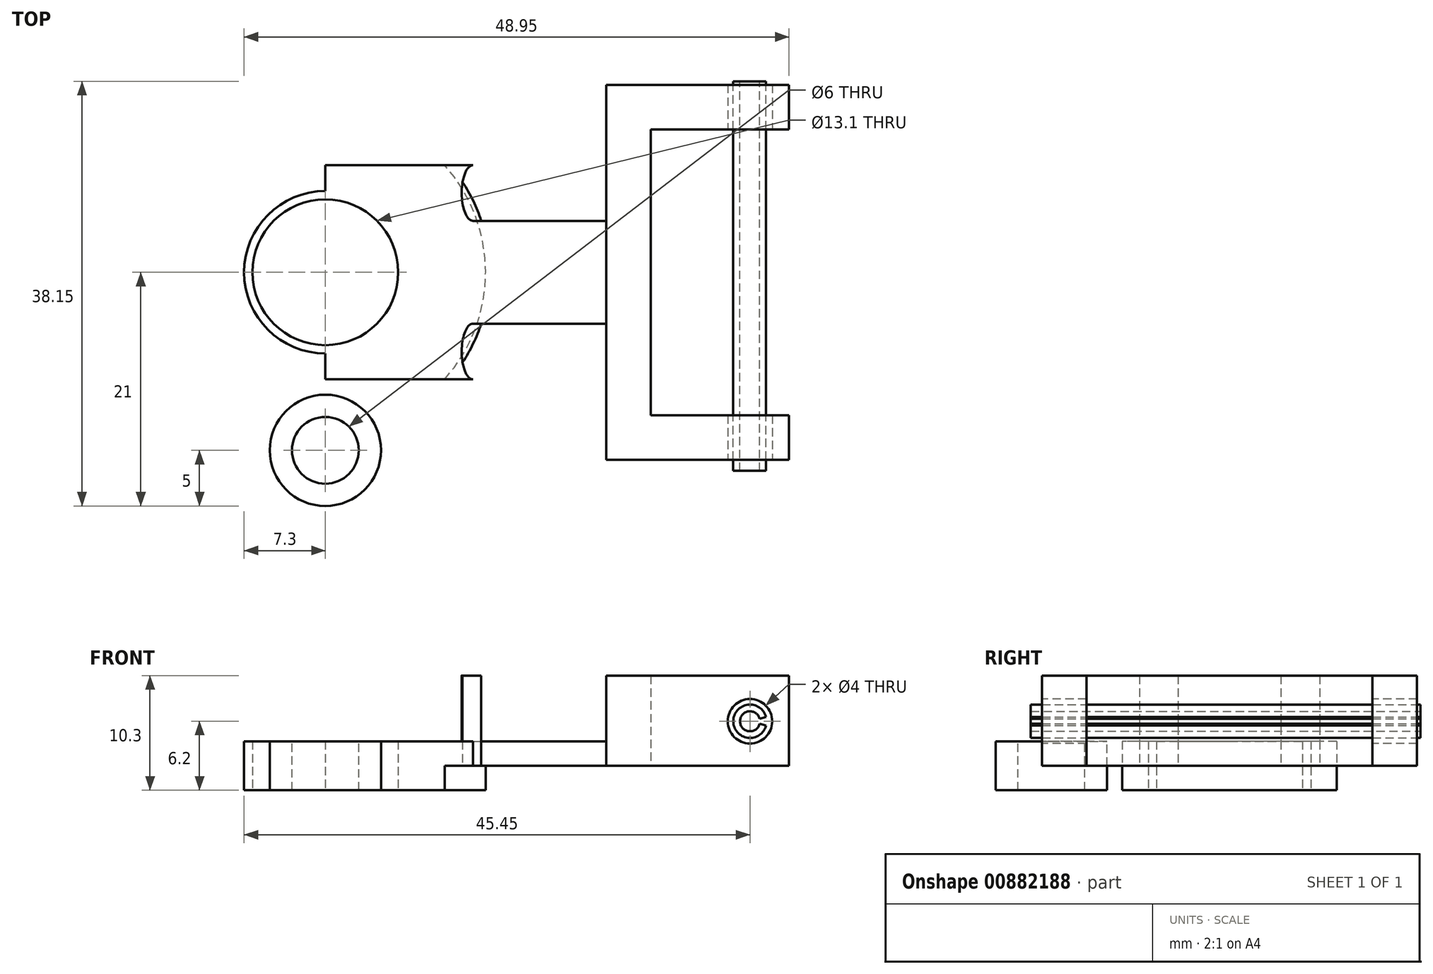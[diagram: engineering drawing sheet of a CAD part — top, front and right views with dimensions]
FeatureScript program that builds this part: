
annotation { "Feature Type Name" : "Feature", "Feature Type Description" : "" }
export const myFeature = defineFeature(function(context is Context, id is Id, definition is map)
    precondition{}
    {
        {
            var Q0;
            Q0=qCreatedBy(makeId("Top.planeOp"),FACE);
            var sketch = newSketch(context, id + "F0", { "sketchPlane" : qUnion([Q0])});
            skCircle(sketch, "E0", {"center": v(0, 0) * mm, "radius": 14.75 * mm});
            skCircle(sketch, "E1", {"center": v(0, 0) * mm, "radius": 14.4 * mm});
            skCircle(sketch, "E2", {"center": v(0, 0) * mm, "radius": 6.55 * mm});
            skCircle(sketch, "E3", {"center": v(0, 0) * mm, "radius": 7.3 * mm});
            skLineSegment(sketch, "E4", {"start": v(0, 0) * mm, "end": v(48.92, 0) * mm, "construction": true});
            skLineSegment(sketch, "E5.bottom", {"start": v(0, 9.62) * mm, "end": v(25.25, 9.62) * mm});
            skLineSegment(sketch, "E5.top", {"start": v(0, -9.62) * mm, "end": v(25.25, -9.62) * mm});
            skLineSegment(sketch, "E5.left", {"start": v(0, 9.62) * mm, "end": v(0, -9.62) * mm});
            skPoint(sketch, "E5.middle", {"position": v(12.63, 0) * mm});
            skLineSegment(sketch, "E6.bottom", {"start": v(25.25, 16.85) * mm, "end": v(41.65, 16.85) * mm});
            skLineSegment(sketch, "E6.top", {"start": v(25.25, -16.85) * mm, "end": v(41.65, -16.85) * mm});
            skLineSegment(sketch, "E6.left", {"start": v(25.25, 16.85) * mm, "end": v(25.25, 9.62) * mm});
            skLineSegment(sketch, "E6.right", {"start": v(41.65, 16.85) * mm, "end": v(41.65, 12.85) * mm});
            skPoint(sketch, "E6.middle", {"position": v(33.45, 0) * mm});
            skLineSegment(sketch, "E7.bottom", {"start": v(29.25, -12.85) * mm, "end": v(41.65, -12.85) * mm});
            skLineSegment(sketch, "E7.top", {"start": v(29.25, 12.85) * mm, "end": v(41.65, 12.85) * mm});
            skLineSegment(sketch, "E7.left", {"start": v(29.25, -12.85) * mm, "end": v(29.25, 12.85) * mm});
            skLineSegment(sketch, "E8.trimOffspring", {"start": v(41.65, -12.85) * mm, "end": v(41.65, -16.85) * mm});
            skLineSegment(sketch, "E9.trimOffspring", {"start": v(25.25, -9.62) * mm, "end": v(25.25, -16.85) * mm});
            skLineSegment(sketch, "E10.bottom", {"start": v(25.25, 9.62) * mm, "end": v(13.25, 9.62) * mm});
            skLineSegment(sketch, "E10.top", {"start": v(25.25, 4.62) * mm, "end": v(13.25, 4.62) * mm});
            skLineSegment(sketch, "E10.left", {"start": v(25.25, 9.62) * mm, "end": v(25.25, 4.62) * mm});
            skLineSegment(sketch, "E10.right", {"start": v(13.25, 9.62) * mm, "end": v(13.25, 4.62) * mm, "construction": true});
            skPoint(sketch, "E11", {"position": v(10.71, 9.63) * mm});
            skPoint(sketch, "E12", {"position": v(11.18, 9.62) * mm});
            skPoint(sketch, "E13", {"position": v(10.71, -9.62) * mm});
            skPoint(sketch, "E14", {"position": v(11.18, -9.62) * mm});
            skLineSegment(sketch, "E15", {"start": v(0, 0) * mm, "end": v(-14.4, 0) * mm, "construction": true});
            skLineSegment(sketch, "E16", {"start": v(-14.4, 0) * mm, "end": v(-14.75, 0) * mm, "construction": true});
            skArc(sketch, "E17", {"start": v(10.71, 9.63) * mm, "mid": v(-14.4, 0) * mm, "end": v(10.71, -9.63) * mm});
            skArc(sketch, "E18", {"start": v(11.18, 9.62) * mm, "mid": v(-14.75, 0) * mm, "end": v(11.18, -9.63) * mm});
            skEllipticalArc(sketch, "E19", {});
            skLineSegment(sketch, "E20.MirrorCS", {"start": v(25.25, -4.62) * mm, "end": v(13.25, -4.62) * mm});
            skEllipticalArc(sketch, "E21.MirrorCS", {});
            skLineSegment(sketch, "E22.MirrorCS", {"start": v(25.25, -9.62) * mm, "end": v(13.25, -9.62) * mm});
            skLineSegment(sketch, "E23.MirrorCS", {"start": v(25.25, -9.62) * mm, "end": v(25.25, -4.62) * mm});
            skLineSegment(sketch, "E24", {"start": v(25.25, 4.62) * mm, "end": v(25.25, -4.62) * mm});
            const initialGuessF0  = {"E19": [0.01325, 0.007125, 0, 1, 0.0025, 0.001, 0, 3.141592653589793], "E21.MirrorCS": [0.01325, -0.007125, 0, -1, 0.0025, 0.001, 3.141592653589793, 0]};
            skSetInitialGuess(sketch, initialGuessF0);
            skSolve(sketch);
        }
        {
            var Q0;
            {var subQ0=sQuery(id+"F0.wireOp",EDGE,"E19");var subQ1=sQuery(id+"F0.wireOp",EDGE,"E0");var subQ2=makeQuery(id+"F0.imprint","INTERSECT",VERTEX,{"derivedFrom":[subQ1,subQ0]});Q0=makeQuery(id+"F0.imprint","IMPRINT",FACE,{"disambiguationData":[TD([[makeQuery(id+"F0.imprint","IMPRINT",EDGE,{"disambiguationData":[TD([[subQ2,1.0]])],"derivedFrom":subQ1}),1.0]])]});}
            var Q1;
            {var subQ0=sQuery(id+"F0.wireOp",EDGE,"E5.bottom");var subQ1=sQuery(id+"F0.wireOp",EDGE,"E0");var subQ2=makeQuery(id+"F0.imprint","INTERSECT",VERTEX,{"derivedFrom":[subQ1,subQ0]});Q1=makeQuery(id+"F0.imprint","IMPRINT",FACE,{"disambiguationData":[TD([[makeQuery(id+"F0.imprint","IMPRINT",EDGE,{"disambiguationData":[TD([[subQ2,1.0]])],"derivedFrom":subQ1}),1.0]])]});}
            var Q2;
            {var subQ0=sQuery(id+"F0.wireOp",EDGE,"E10.top");var subQ1=sQuery(id+"F0.wireOp",EDGE,"E0");var subQ2=makeQuery(id+"F0.imprint","INTERSECT",VERTEX,{"derivedFrom":[subQ1,subQ0]});Q2=makeQuery(id+"F0.imprint","IMPRINT",FACE,{"disambiguationData":[TD([[makeQuery(id+"F0.imprint","IMPRINT",EDGE,{"disambiguationData":[TD([[subQ2,1.0]])],"derivedFrom":subQ1}),1.0]])]});}
            var Q3;
            {var subQ0=sQuery(id+"F0.wireOp",EDGE,"E21.MirrorCS");var subQ1=sQuery(id+"F0.wireOp",EDGE,"E0");var subQ2=makeQuery(id+"F0.imprint","INTERSECT",VERTEX,{"derivedFrom":[subQ1,subQ0]});Q3=makeQuery(id+"F0.imprint","IMPRINT",FACE,{"disambiguationData":[TD([[makeQuery(id+"F0.imprint","IMPRINT",EDGE,{"disambiguationData":[TD([[subQ2,-1.0]])],"derivedFrom":subQ1}),1.0]])]});}
            var Q4;
            {var subQ0=sQuery(id+"F0.wireOp",EDGE,"E5.top");var subQ1=sQuery(id+"F0.wireOp",EDGE,"E0");var subQ2=makeQuery(id+"F0.imprint","INTERSECT",VERTEX,{"derivedFrom":[subQ1,subQ0]});Q4=makeQuery(id+"F0.imprint","IMPRINT",FACE,{"disambiguationData":[TD([[makeQuery(id+"F0.imprint","IMPRINT",EDGE,{"disambiguationData":[TD([[subQ2,-1.0]])],"derivedFrom":subQ1}),1.0]])]});}
            var Q5;
            {var subQ0=sQuery(id+"F0.wireOp",EDGE,"E5.bottom");var subQ1=sQuery(id+"F0.wireOp",EDGE,"E0");var subQ2=makeQuery(id+"F0.imprint","INTERSECT",VERTEX,{"derivedFrom":[subQ1,subQ0]});Q5=makeQuery(id+"F0.imprint","IMPRINT",FACE,{"disambiguationData":[TD([[makeQuery(id+"F0.imprint","IMPRINT",EDGE,{"disambiguationData":[TD([[subQ2,-1.0]])],"derivedFrom":subQ1}),1.0]])]});}
            var Q6;
            {var subQ0=sQuery(id+"F0.wireOp",EDGE,"E19");var subQ3=sQuery(id+"F0.wireOp",EDGE,"E1");var subQ4=makeQuery(id+"F0.imprint","INTERSECT",VERTEX,{"derivedFrom":[subQ3,subQ0]});Q6=makeQuery(id+"F0.imprint","IMPRINT",FACE,{"disambiguationData":[TD([[makeQuery(id+"F0.imprint","IMPRINT",EDGE,{"disambiguationData":[TD([[subQ4,-1.0]])],"derivedFrom":subQ3}),1.0]])]});}
            var Q7;
            {var subQ0=sQuery(id+"F0.wireOp",EDGE,"E19");var subQ1=sQuery(id+"F0.wireOp",EDGE,"E1");var subQ2=makeQuery(id+"F0.imprint","INTERSECT",VERTEX,{"derivedFrom":[subQ1,subQ0]});Q7=makeQuery(id+"F0.imprint","IMPRINT",FACE,{"disambiguationData":[TD([[makeQuery(id+"F0.imprint","IMPRINT",EDGE,{"disambiguationData":[TD([[subQ2,1.0]])],"derivedFrom":subQ1}),1.0]])]});}
            var Q8;
            {var subQ0=sQuery(id+"F0.wireOp",EDGE,"E21.MirrorCS");var subQ1=sQuery(id+"F0.wireOp",EDGE,"E1");var subQ2=makeQuery(id+"F0.imprint","INTERSECT",VERTEX,{"derivedFrom":[subQ1,subQ0]});Q8=makeQuery(id+"F0.imprint","IMPRINT",FACE,{"disambiguationData":[TD([[makeQuery(id+"F0.imprint","IMPRINT",EDGE,{"disambiguationData":[TD([[subQ2,-1.0]])],"derivedFrom":subQ1}),1.0]])]});}
            var Q9;
            {var subQ1=sQuery(id+"F0.wireOp",EDGE,"E5.bottom");var subQ3=sQuery(id+"F0.wireOp",EDGE,"E1");var subQ4=makeQuery(id+"F0.imprint","INTERSECT",VERTEX,{"derivedFrom":[subQ3,subQ1]});Q9=makeQuery(id+"F0.imprint","IMPRINT",FACE,{"disambiguationData":[TD([[makeQuery(id+"F0.imprint","IMPRINT",EDGE,{"disambiguationData":[TD([[subQ4,-1.0]])],"derivedFrom":subQ3}),1.0]])]});}
            var Q10;
            {var subQ0=sQuery(id+"F0.wireOp",EDGE,"E5.left");var subQ1=sQuery(id+"F0.wireOp",EDGE,"E2");var subQ2=makeQuery(id+"F0.imprint","INTERSECT",VERTEX,{"disambiguationData":[OD(0.0)],"derivedFrom":[subQ1,subQ0]});Q10=makeQuery(id+"F0.imprint","IMPRINT",FACE,{"disambiguationData":[TD([[makeQuery(id+"F0.imprint","IMPRINT",EDGE,{"disambiguationData":[TD([[subQ2,-1.0]])],"derivedFrom":subQ1}),-1.0]])]});}
            var Q11;
            {var subQ0=sQuery(id+"F0.wireOp",EDGE,"E5.left");var subQ1=sQuery(id+"F0.wireOp",EDGE,"E2");var subQ2=makeQuery(id+"F0.imprint","INTERSECT",VERTEX,{"disambiguationData":[OD(0.0)],"derivedFrom":[subQ1,subQ0]});Q11=makeQuery(id+"F0.imprint","IMPRINT",FACE,{"disambiguationData":[TD([[makeQuery(id+"F0.imprint","IMPRINT",EDGE,{"disambiguationData":[TD([[subQ2,1.0]])],"derivedFrom":subQ1}),-1.0]])]});}
            extrude(context, id + "F1", {"entities" : qUnion([Q0, Q1, Q2, Q3, Q4, Q5, Q6, Q7, Q8, Q9, Q10, Q11]), "depth" : 2.2 * mm, "offsetDistance" : 25 * mm});
        }
        {
            var Q0;
            Q0=makeQuery(id+"F0.imprint","IMPRINT",FACE,{"disambiguationData":[TD([[makeQuery(id+"F0.imprint","IMPRINT",EDGE,{"derivedFrom":sQuery(id+"F0.wireOp",EDGE,"E1")}),1.0]])]});
            var Q1;
            {var subQ0=sQuery(id+"F0.wireOp",EDGE,"E21.MirrorCS");var subQ1=sQuery(id+"F0.wireOp",EDGE,"E1");var subQ2=makeQuery(id+"F0.imprint","INTERSECT",VERTEX,{"derivedFrom":[subQ1,subQ0]});Q1=makeQuery(id+"F0.imprint","IMPRINT",FACE,{"disambiguationData":[TD([[makeQuery(id+"F0.imprint","IMPRINT",EDGE,{"disambiguationData":[TD([[subQ2,-1.0]])],"derivedFrom":subQ1}),1.0]])]});}
            var Q2;
            {var subQ0=sQuery(id+"F0.wireOp",EDGE,"E19");var subQ1=sQuery(id+"F0.wireOp",EDGE,"E1");var subQ2=makeQuery(id+"F0.imprint","INTERSECT",VERTEX,{"derivedFrom":[subQ1,subQ0]});Q2=makeQuery(id+"F0.imprint","IMPRINT",FACE,{"disambiguationData":[TD([[makeQuery(id+"F0.imprint","IMPRINT",EDGE,{"disambiguationData":[TD([[subQ2,1.0]])],"derivedFrom":subQ1}),1.0]])]});}
            var Q3;
            {var subQ1=sQuery(id+"F0.wireOp",EDGE,"E5.bottom");var subQ3=sQuery(id+"F0.wireOp",EDGE,"E1");var subQ4=makeQuery(id+"F0.imprint","INTERSECT",VERTEX,{"derivedFrom":[subQ3,subQ1]});Q3=makeQuery(id+"F0.imprint","IMPRINT",FACE,{"disambiguationData":[TD([[makeQuery(id+"F0.imprint","IMPRINT",EDGE,{"disambiguationData":[TD([[subQ4,-1.0]])],"derivedFrom":subQ3}),1.0]])]});}
            var Q4;
            {var subQ0=sQuery(id+"F0.wireOp",EDGE,"E5.left");var subQ1=sQuery(id+"F0.wireOp",EDGE,"E2");var subQ2=makeQuery(id+"F0.imprint","INTERSECT",VERTEX,{"disambiguationData":[OD(0.0)],"derivedFrom":[subQ1,subQ0]});Q4=makeQuery(id+"F0.imprint","IMPRINT",FACE,{"disambiguationData":[TD([[makeQuery(id+"F0.imprint","IMPRINT",EDGE,{"disambiguationData":[TD([[subQ2,-1.0]])],"derivedFrom":subQ1}),-1.0]])]});}
            var Q5;
            {var subQ0=sQuery(id+"F0.wireOp",EDGE,"E5.left");var subQ1=sQuery(id+"F0.wireOp",EDGE,"E2");var subQ2=makeQuery(id+"F0.imprint","INTERSECT",VERTEX,{"disambiguationData":[OD(0.0)],"derivedFrom":[subQ1,subQ0]});Q5=makeQuery(id+"F0.imprint","IMPRINT",FACE,{"disambiguationData":[TD([[makeQuery(id+"F0.imprint","IMPRINT",EDGE,{"disambiguationData":[TD([[subQ2,1.0]])],"derivedFrom":subQ1}),-1.0]])]});}
            extrude(context, id + "F2", {"entities" : qUnion([Q0, Q1, Q2, Q3, Q4, Q5]), "operationType" : NewBodyOperationType.ADD, "oppositeDirection" : true, "depth" : 2.2 * mm, "offsetDistance" : 25 * mm});
        }
        {
            var Q0;
            {var subQ0=sQuery(id+"F0.wireOp",EDGE,"E5.bottom");var subQ1=sQuery(id+"F0.wireOp",EDGE,"E0");var subQ2=makeQuery(id+"F0.imprint","INTERSECT",VERTEX,{"derivedFrom":[subQ1,subQ0]});Q0=makeQuery(id+"F0.imprint","IMPRINT",FACE,{"disambiguationData":[TD([[makeQuery(id+"F0.imprint","IMPRINT",EDGE,{"disambiguationData":[TD([[subQ2,1.0]])],"derivedFrom":subQ1}),-1.0]])]});}
            var Q1;
            {var subQ4=sQuery(id+"F0.wireOp",EDGE,"E10.bottom");Q1=makeQuery(id+"F0.imprint","IMPRINT",FACE,{"disambiguationData":[TD([[makeQuery(id+"F0.imprint","IMPRINT",EDGE,{"derivedFrom":subQ4}),1.0]])]});}
            var Q2;
            Q2=makeQuery(id+"F0.imprint","IMPRINT",FACE,{"disambiguationData":[TD([[makeQuery(id+"F0.imprint","IMPRINT",EDGE,{"derivedFrom":sQuery(id+"F0.wireOp",EDGE,"E6.bottom")}),-1.0]])]});
            var Q3;
            {var subQ0=sQuery(id+"F0.wireOp",EDGE,"E22.MirrorCS");Q3=makeQuery(id+"F0.imprint","IMPRINT",FACE,{"disambiguationData":[TD([[makeQuery(id+"F0.imprint","IMPRINT",EDGE,{"derivedFrom":subQ0}),-1.0]])]});}
            var Q4;
            {var subQ0=sQuery(id+"F0.wireOp",EDGE,"E5.top");var subQ1=sQuery(id+"F0.wireOp",EDGE,"E0");var subQ2=makeQuery(id+"F0.imprint","INTERSECT",VERTEX,{"derivedFrom":[subQ1,subQ0]});Q4=makeQuery(id+"F0.imprint","IMPRINT",FACE,{"disambiguationData":[TD([[makeQuery(id+"F0.imprint","IMPRINT",EDGE,{"disambiguationData":[TD([[subQ2,-1.0]])],"derivedFrom":subQ1}),-1.0]])]});}
            var Q5;
            {var subQ5=sQuery(id+"F0.wireOp",EDGE,"E24");Q5=makeQuery(id+"F0.imprint","IMPRINT",FACE,{"disambiguationData":[TD([[makeQuery(id+"F0.imprint","IMPRINT",EDGE,{"derivedFrom":subQ5}),-1.0]])]});}
            extrude(context, id + "F3", {"entities" : qUnion([Q0, Q1, Q2, Q3, Q4, Q5]), "operationType" : NewBodyOperationType.ADD, "depth" : 2.2 * mm, "offsetDistance" : 25 * mm});
        }
        {
            var Q0;
            {var subQ0=sQuery(id+"F0.wireOp",EDGE,"E22.MirrorCS");Q0=makeQuery(id+"F0.imprint","IMPRINT",FACE,{"disambiguationData":[TD([[makeQuery(id+"F0.imprint","IMPRINT",EDGE,{"derivedFrom":subQ0}),-1.0]])]});}
            var Q1;
            {var subQ0=sQuery(id+"F0.wireOp",EDGE,"E21.MirrorCS");var subQ1=sQuery(id+"F0.wireOp",EDGE,"E0");var subQ2=makeQuery(id+"F0.imprint","INTERSECT",VERTEX,{"derivedFrom":[subQ1,subQ0]});Q1=makeQuery(id+"F0.imprint","IMPRINT",FACE,{"disambiguationData":[TD([[makeQuery(id+"F0.imprint","IMPRINT",EDGE,{"disambiguationData":[TD([[subQ2,-1.0]])],"derivedFrom":subQ1}),1.0]])]});}
            var Q2;
            {var subQ0=sQuery(id+"F0.wireOp",EDGE,"E21.MirrorCS");var subQ1=sQuery(id+"F0.wireOp",EDGE,"E1");var subQ2=makeQuery(id+"F0.imprint","INTERSECT",VERTEX,{"derivedFrom":[subQ1,subQ0]});Q2=makeQuery(id+"F0.imprint","IMPRINT",FACE,{"disambiguationData":[TD([[makeQuery(id+"F0.imprint","IMPRINT",EDGE,{"disambiguationData":[TD([[subQ2,-1.0]])],"derivedFrom":subQ1}),1.0]])]});}
            var Q3;
            {var subQ0=sQuery(id+"F0.wireOp",EDGE,"E19");var subQ1=sQuery(id+"F0.wireOp",EDGE,"E0");var subQ2=makeQuery(id+"F0.imprint","INTERSECT",VERTEX,{"derivedFrom":[subQ1,subQ0]});Q3=makeQuery(id+"F0.imprint","IMPRINT",FACE,{"disambiguationData":[TD([[makeQuery(id+"F0.imprint","IMPRINT",EDGE,{"disambiguationData":[TD([[subQ2,1.0]])],"derivedFrom":subQ1}),1.0]])]});}
            var Q4;
            {var subQ0=sQuery(id+"F0.wireOp",EDGE,"E19");var subQ1=sQuery(id+"F0.wireOp",EDGE,"E1");var subQ2=makeQuery(id+"F0.imprint","INTERSECT",VERTEX,{"derivedFrom":[subQ1,subQ0]});Q4=makeQuery(id+"F0.imprint","IMPRINT",FACE,{"disambiguationData":[TD([[makeQuery(id+"F0.imprint","IMPRINT",EDGE,{"disambiguationData":[TD([[subQ2,1.0]])],"derivedFrom":subQ1}),1.0]])]});}
            var Q5;
            {var subQ4=sQuery(id+"F0.wireOp",EDGE,"E10.bottom");Q5=makeQuery(id+"F0.imprint","IMPRINT",FACE,{"disambiguationData":[TD([[makeQuery(id+"F0.imprint","IMPRINT",EDGE,{"derivedFrom":subQ4}),1.0]])]});}
            extrude(context, id + "F4", {"entities" : qUnion([Q0, Q1, Q2, Q3, Q4, Q5]), "operationType" : NewBodyOperationType.ADD, "depth" : 8.1 * mm, "offsetDistance" : 25 * mm});
        }
        {
            var Q0;
            Q0=makeQuery(id+"F0.imprint","IMPRINT",FACE,{"disambiguationData":[TD([[makeQuery(id+"F0.imprint","IMPRINT",EDGE,{"derivedFrom":sQuery(id+"F0.wireOp",EDGE,"E6.bottom")}),-1.0]])]});
            extrude(context, id + "F5", {"entities" : qUnion([Q0]), "operationType" : NewBodyOperationType.ADD, "depth" : 8.1 * mm, "offsetDistance" : 25 * mm});
        }
        {
            var Q0;
            {var subQ0=sQuery(id+"F0.wireOp",EDGE,"E6.top");Q0=makeQuery(id+"F5.boolean.opBoolean","MERGE",FACE,{"derivedFrom":[makeQuery(id+"F3.opExtrude","SWEPT_FACE",FACE,{"disambiguationData":[OSD([subQ0])]}),makeQuery(id+"F5.opExtrude","SWEPT_FACE",FACE,{"disambiguationData":[OSD([subQ0])]})]});}
            var sketch = newSketch(context, id + "F6", { "sketchPlane" : qUnion([Q0])});
            skCircle(sketch, "E25", {"center": v(38.15, 4) * mm, "radius": 2 * mm});
            skSolve(sketch);
        }
        {
            var Q0;
            Q0 = qSketchRegion(id + "F6", true);
            extrude(context, id + "F7", {"entities" : qUnion([Q0]), "operationType" : NewBodyOperationType.REMOVE, "endBound" : BoundingType.THROUGH_ALL, "oppositeDirection" : true, "depth" : 25 * mm, "offsetDistance" : 25 * mm});
        }
        {
            var Q0;
            {var subQ0=sQuery(id+"F0.wireOp",EDGE,"E6.top");Q0=makeQuery(id+"F5.boolean.opBoolean","MERGE",FACE,{"derivedFrom":[makeQuery(id+"F3.opExtrude","SWEPT_FACE",FACE,{"disambiguationData":[OSD([subQ0])]}),makeQuery(id+"F5.opExtrude","SWEPT_FACE",FACE,{"disambiguationData":[OSD([subQ0])]})]});}
            var sketch = newSketch(context, id + "F8", { "sketchPlane" : qUnion([Q0])});
            skArc(sketch, "E26", {"start": v(39.6, 4.39) * mm, "mid": v(36.65, 4) * mm, "end": v(39.6, 3.61) * mm});
            skArc(sketch, "E27", {"start": v(39.02, 4.23) * mm, "mid": v(37.25, 4) * mm, "end": v(39.02, 3.77) * mm});
            skLineSegment(sketch, "E28", {"start": v(38.15, 4) * mm, "end": v(39.96, 4) * mm, "construction": true});
            skLineSegment(sketch, "E29", {"start": v(39.96, 4.48) * mm, "end": v(38.15, 4) * mm});
            skLineSegment(sketch, "E30", {"start": v(38.15, 4) * mm, "end": v(39.96, 3.52) * mm});
            skSolve(sketch);
        }
        {
            var Q0;
            {var subQ0=sQuery(id+"F8.wireOp",EDGE,"E26");Q0=makeQuery(id+"F8.imprint","IMPRINT",FACE,{"disambiguationData":[TD([[makeQuery(id+"F8.imprint","IMPRINT",EDGE,{"derivedFrom":subQ0}),1.0]])]});}
            extrude(context, id + "F9", {"entities" : qUnion([Q0]), "depth" : 1 * mm, "offsetDistance" : 25 * mm, "hasSecondDirection" : true, "secondDirectionOppositeDirection" : true, "secondDirectionDepth" : 34 * mm});
        }
        {
            var Q0;
            {var subQ0=sQuery(id+"F0.wireOp",EDGE,"E0");Q0=makeQuery(id+"F3.boolean.opBoolean","MERGE",FACE,{"derivedFrom":[makeQuery(id+"F1.opExtrude","CAP_FACE",FACE,{"disambiguationData":[OSD([subQ0,sQuery(id+"F0.wireOp",EDGE,"E2")])],"isStart":false}),makeQuery(id+"F3.opExtrude","CAP_FACE",FACE,{"disambiguationData":[OSD([subQ0,sQuery(id+"F0.wireOp",EDGE,"E5.bottom"),sQuery(id+"F0.wireOp",EDGE,"E5.top"),sQuery(id+"F0.wireOp",EDGE,"E6.bottom"),sQuery(id+"F0.wireOp",EDGE,"E6.top"),sQuery(id+"F0.wireOp",EDGE,"E6.left"),sQuery(id+"F0.wireOp",EDGE,"E6.right"),sQuery(id+"F0.wireOp",EDGE,"E7.bottom"),sQuery(id+"F0.wireOp",EDGE,"E7.top"),sQuery(id+"F0.wireOp",EDGE,"E7.left"),sQuery(id+"F0.wireOp",EDGE,"E8.trimOffspring"),sQuery(id+"F0.wireOp",EDGE,"E9.trimOffspring"),sQuery(id+"F0.wireOp",EDGE,"E10.bottom"),sQuery(id+"F0.wireOp",EDGE,"E22.MirrorCS")])],"isStart":false})]});}
            var sketch = newSketch(context, id + "F10", { "sketchPlane" : qUnion([Q0])});
            skCircle(sketch, "E31", {"center": v(0, 0) * mm, "radius": 14.75 * mm, "construction": true});
            skLineSegment(sketch, "E32", {"start": v(0, 0) * mm, "end": v(0, -24.4) * mm, "construction": true});
            skCircle(sketch, "E33", {"center": v(0, -16) * mm, "radius": 3 * mm});
            skCircle(sketch, "E34", {"center": v(0, -16) * mm, "radius": 5 * mm});
            skSolve(sketch);
        }
        {
            var Q0;
            {var subQ0=sQuery(id+"F10.wireOp",EDGE,"E33");var subQ1=makeQuery(id+"F1.opExtrude","CAP_EDGE",EDGE,{"disambiguationData":[OSD([sQuery(id+"F0.wireOp",EDGE,"E0")])],"isStart":false});var subQ2=makeQuery(id+"F10.imprint","INTERSECT",VERTEX,{"disambiguationData":[OD(0.0)],"derivedFrom":[subQ1,subQ0]});Q0=makeQuery(id+"F10.imprint","IMPRINT",FACE,{"disambiguationData":[TD([[makeQuery(id+"F10.imprint","IMPRINT",EDGE,{"disambiguationData":[TD([[subQ2,1.0]])],"derivedFrom":subQ0}),-1.0]])]});}
            var Q1;
            {var subQ0=sQuery(id+"F10.wireOp",EDGE,"E33");var subQ1=makeQuery(id+"F1.opExtrude","CAP_EDGE",EDGE,{"disambiguationData":[OSD([sQuery(id+"F0.wireOp",EDGE,"E0")])],"isStart":false});var subQ2=makeQuery(id+"F10.imprint","INTERSECT",VERTEX,{"disambiguationData":[OD(0.0)],"derivedFrom":[subQ1,subQ0]});Q1=makeQuery(id+"F10.imprint","IMPRINT",FACE,{"disambiguationData":[TD([[makeQuery(id+"F10.imprint","IMPRINT",EDGE,{"disambiguationData":[TD([[subQ2,-1.0]])],"derivedFrom":subQ0}),-1.0]])]});}
            var Q2;
            Q2=makeQuery(id+"F2.opExtrude","CAP_FACE",FACE,{"disambiguationData":[OSD([sQuery(id+"F0.wireOp",EDGE,"E1"),sQuery(id+"F0.wireOp",EDGE,"E2")])],"isStart":false});
            extrude(context, id + "F11", {"entities" : qUnion([Q0, Q1]), "operationType" : NewBodyOperationType.ADD, "endBound" : BoundingType.UP_TO_SURFACE, "oppositeDirection" : true, "depth" : 25 * mm, "endBoundEntityFace" : qUnion([Q2]), "offsetDistance" : 25 * mm});
        }
        {
            var Q0;
            {var subQ0=sQuery(id+"F10.wireOp",EDGE,"E33");var subQ1=makeQuery(id+"F1.opExtrude","CAP_EDGE",EDGE,{"disambiguationData":[OSD([sQuery(id+"F0.wireOp",EDGE,"E0")])],"isStart":false});var subQ2=makeQuery(id+"F10.imprint","INTERSECT",VERTEX,{"disambiguationData":[OD(0.0)],"derivedFrom":[subQ1,subQ0]});Q0=makeQuery(id+"F10.imprint","IMPRINT",FACE,{"disambiguationData":[TD([[makeQuery(id+"F10.imprint","IMPRINT",EDGE,{"disambiguationData":[TD([[subQ2,1.0]])],"derivedFrom":subQ0}),1.0]])]});}
            var Q1;
            Q1=makeQuery(id+"F11.boolean.opBoolean","MERGE",FACE,{"derivedFrom":[makeQuery(id+"F2.opExtrude","CAP_FACE",FACE,{"disambiguationData":[OSD([sQuery(id+"F0.wireOp",EDGE,"E1"),sQuery(id+"F0.wireOp",EDGE,"E2")])],"isStart":false}),makeQuery(id+"F11.opExtrude","CAP_FACE",FACE,{"disambiguationData":[OSD([sQuery(id+"F10.wireOp",EDGE,"E33"),sQuery(id+"F10.wireOp",EDGE,"E34")])],"isStart":false})]});
            extrude(context, id + "F12", {"entities" : qUnion([Q0]), "operationType" : NewBodyOperationType.REMOVE, "endBound" : BoundingType.UP_TO_SURFACE, "oppositeDirection" : true, "depth" : 25 * mm, "endBoundEntityFace" : qUnion([Q1]), "offsetDistance" : 25 * mm});
        }
    });
